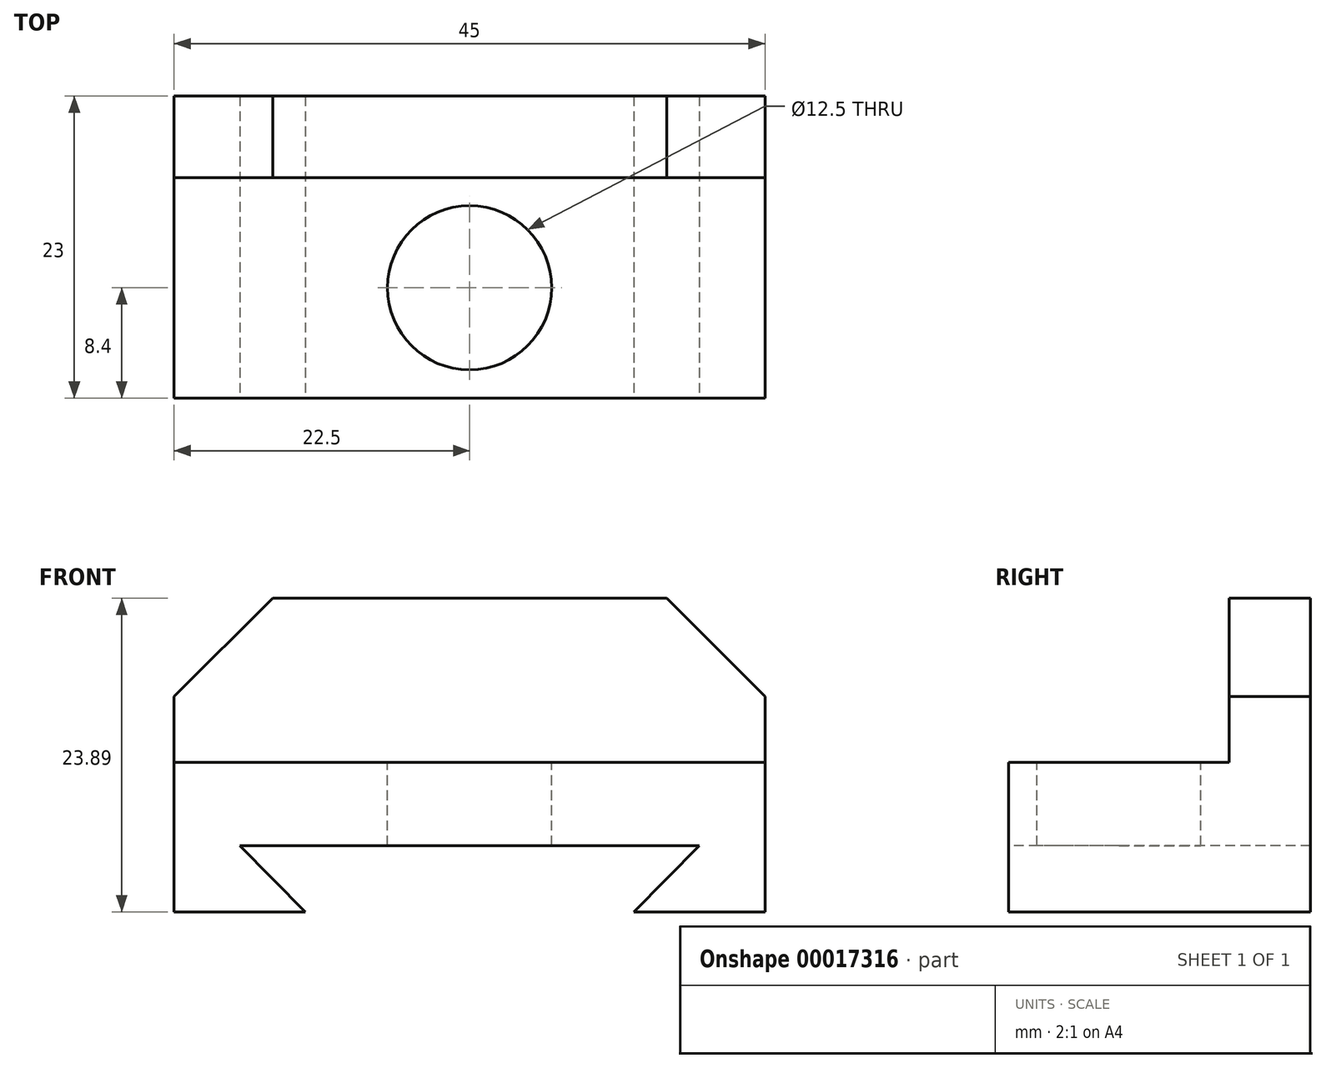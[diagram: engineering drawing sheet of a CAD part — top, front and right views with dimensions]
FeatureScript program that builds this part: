
annotation { "Feature Type Name" : "Feature", "Feature Type Description" : "" }
export const myFeature = defineFeature(function(context is Context, id is Id, definition is map)
    precondition{}
    {
        {
            var Q0;
            Q0=qCreatedBy(makeId("Front.planeOp"),FACE);
            var sketch = newSketch(context, id + "F0", { "sketchPlane" : qUnion([Q0])});
            skLineSegment(sketch, "E0.bottom", {"start": v(0, 0) * mm, "end": v(-45, 0) * mm});
            skLineSegment(sketch, "E0.top", {"start": v(-7.5, 23.89) * mm, "end": v(-37.5, 23.89) * mm});
            skLineSegment(sketch, "E0.right", {"start": v(-45, 0) * mm, "end": v(-45, 11.39) * mm});
            skLineSegment(sketch, "E1", {"start": v(-45, 11.39) * mm, "end": v(0, 11.39) * mm});
            skPoint(sketch, "E2.end.orphan", {"position": v(-22.5, 11.39) * mm});
            skPoint(sketch, "E2.start.orphan", {"position": v(-22.5, 0) * mm});
            skPoint(sketch, "E3.orphan", {"position": v(0, 23.89) * mm});
            skLineSegment(sketch, "E4", {"start": v(0, 0) * mm, "end": v(0, 11.39) * mm});
            skLineSegment(sketch, "E5", {"start": v(0, 11.39) * mm, "end": v(0, 16.39) * mm});
            skLineSegment(sketch, "E6", {"start": v(0, 16.39) * mm, "end": v(-7.5, 23.89) * mm});
            skLineSegment(sketch, "E7", {"start": v(-45, 11.39) * mm, "end": v(-45, 16.39) * mm});
            skLineSegment(sketch, "E8", {"start": v(-45, 16.39) * mm, "end": v(-37.5, 23.89) * mm});
            skSolve(sketch);
        }
        {
            var Q0;
            Q0=makeQuery(id+"F0.imprint","IMPRINT",FACE,{"disambiguationData":[TD([[makeQuery(id+"F0.imprint","IMPRINT",EDGE,{"derivedFrom":sQuery(id+"F0.wireOp",EDGE,"E0.bottom")}),-1.0]])]});
            var Q1;
            Q1=makeQuery(id+"F0.imprint","IMPRINT",FACE,{"disambiguationData":[TD([[makeQuery(id+"F0.imprint","IMPRINT",EDGE,{"derivedFrom":sQuery(id+"F0.wireOp",EDGE,"E1")}),1.0]])]});
            extrude(context, id + "F1", {"entities" : qUnion([Q0, Q1]), "oppositeDirection" : true, "depth" : 23 * mm});
        }
        {
            var Q0;
            Q0=makeQuery(id+"F0.imprint","IMPRINT",FACE,{"disambiguationData":[TD([[makeQuery(id+"F0.imprint","IMPRINT",EDGE,{"derivedFrom":sQuery(id+"F0.wireOp",EDGE,"E1")}),1.0]])]});
            extrude(context, id + "F2", {"entities" : qUnion([Q0]), "operationType" : NewBodyOperationType.REMOVE, "oppositeDirection" : true, "depth" : 16.8 * mm});
        }
        {
            var Q0;
            Q0=makeQuery(id+"F1.opExtrude","CAP_FACE",FACE,{"disambiguationData":[OSD([sQuery(id+"F0.wireOp",EDGE,"E0.bottom"),sQuery(id+"F0.wireOp",EDGE,"E0.right"),sQuery(id+"F0.wireOp",EDGE,"0f8a9dea-0f71-42f3-8ea6-3132081163bd"),sQuery(id+"F0.wireOp",EDGE,"E0.top"),sQuery(id+"F0.wireOp",EDGE,"E4"),sQuery(id+"F0.wireOp",EDGE,"190cc529-9600-4850-a4c9-81cfab8153f8")])],"isStart":true});
            var sketch = newSketch(context, id + "F3", { "sketchPlane" : qUnion([Q0])});
            skLineSegment(sketch, "E9", {"start": v(-35, 0) * mm, "end": v(-40, 5.05) * mm});
            skLineSegment(sketch, "E10", {"start": v(-40, 5.05) * mm, "end": v(-5, 5.05) * mm});
            skLineSegment(sketch, "E11", {"start": v(-5, 5.05) * mm, "end": v(-10, 0) * mm});
            skLineSegment(sketch, "E12", {"start": v(-35, 0) * mm, "end": v(-10, 0) * mm});
            skSolve(sketch);
        }
        {
            var Q0;
            Q0=makeQuery(id+"F3.imprint","IMPRINT",FACE,{"disambiguationData":[TD([[makeQuery(id+"F3.imprint","IMPRINT",EDGE,{"derivedFrom":sQuery(id+"F3.wireOp",EDGE,"E9")}),-1.0]])]});
            extrude(context, id + "F4", {"entities" : qUnion([Q0]), "operationType" : NewBodyOperationType.REMOVE, "oppositeDirection" : true, "depth" : 25 * mm});
        }
        {
            var Q0;
            Q0=makeQuery(id+"F2.boolean.opBoolean","COPY",FACE,{"derivedFrom":makeQuery(id+"F2.opExtrude","SWEPT_FACE",FACE,{"disambiguationData":[OSD([sQuery(id+"F0.wireOp",EDGE,"E1")])]})});
            var sketch = newSketch(context, id + "F5", { "sketchPlane" : qUnion([Q0])});
            skCircle(sketch, "E13", {"center": v(-22.5, 8.4) * mm, "radius": 6.25 * mm});
            skSolve(sketch);
        }
        {
            var Q0;
            Q0=makeQuery(id+"F5.imprint","IMPRINT",FACE,{"disambiguationData":[TD([[makeQuery(id+"F5.imprint","IMPRINT",EDGE,{"derivedFrom":sQuery(id+"F5.wireOp",EDGE,"E13")}),1.0]])]});
            extrude(context, id + "F6", {"entities" : qUnion([Q0]), "operationType" : NewBodyOperationType.REMOVE, "oppositeDirection" : true, "depth" : 25 * mm});
        }
    });
